# Revit family: Haworth_Epure_RectangularDesk_EU_PRELIMINARY
name_source: partatom
category: Furniture
units: mm (PartAtom-declared; Revit-internal decimal feet)

## family parameters
Always vertical = Yes
Cut with Voids When Loaded = No
OmniClass Number = 23.40.70.14.64.11
OmniClass Title = Office Furniture
Room Calculation Point = No
Shared = No
Work Plane-Based = No

## types (8) — shared parameters
Actual Height = 73 cm
Assembly Code = E2020200
Description = Haworth - Epure - Rectangular Desk
Flip Top Finish = Haworth _ Paint _ Metallic Silver
Leg Height = 70 cm
Manufacturer = Haworth
Model = EURD1XXX
Revision Number = 1
Size = Verify Final Dim.w/ Haworth
Storage Options = Actual Width > 100 cm
Suspended Pedestal Open with Box Files = No
Suspended Pedestal Open with Pencil = No
Trim Finish = Haworth _ Metal _ Structured White EC
URL = https://www.haworth.com
URL - Product = https://www.haworth.com
Warranty = http://www.haworth.com
Worksurface Depth = 60, 80, 90, 100 cm
Worksurface Width = 60, 80, 100, 120, 140, 160, 180 cm

## per-type parameters (varying)
| type | Accessory Kit | Actual Depth | Actual Width | Casters | Flip Top Cable Outlet | Mobile Pedestal | Mobile Pedestal Hinged Door | Mobile Pedestal Sliding Door | No Accessory Kit | No Casters | Rectangle | Round Cable Outlet | Rounded Corners | Scallop | Security Drawer | Squared Corners | Suspended Pedestal | Suspended Pedestal Open | Void Depth |
| 60 x 60 | No | 60 cm | 60 cm | Yes | No | No | No | No | Yes | No | Yes | No | No | No | No | Yes | No | No | 0 cm |
| 80 x 80 | No | 80 cm | 80 cm | No | No | No | No | No | Yes | Yes | No | No | No | Yes | No | Yes | No | No | 3 cm |
| 140 x 90 | Yes | 90 cm | 140 cm | Yes | Yes | Yes | Yes | No | No | No | No | No | Yes | Yes | No | No | No | No | 3 cm |
| 180 x 100 | Yes | 100 cm | 180 cm | No | Yes | No | No | No | No | Yes | No | No | No | Yes | Yes | Yes | No | No | 3 cm |
| 160 x 100 | Yes | 100 cm | 160 cm | No | No | Yes | No | Yes | No | Yes | Yes | Yes | No | No | No | Yes | No | No | 0 cm |
| 180 x 90 | Yes | 90 cm | 180 cm | No | Yes | No | No | No | No | Yes | Yes | No | Yes | No | No | No | Yes | Yes | 0 cm |
| 180 x 80 | Yes | 80 cm | 180 cm | Yes | No | No | No | No | No | No | No | Yes | No | Yes | No | Yes | Yes | Yes | 3 cm |
| 140 x 60 | No | 60 cm | 140 cm | No | No | No | No | No | Yes | Yes | Yes | No | No | No | No | Yes | No | No | 0 cm |

## geometry (parser evidence)
native form markers: Blend x8, Sweep x21
no freeform markers — native parametric forms only
